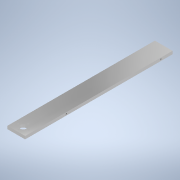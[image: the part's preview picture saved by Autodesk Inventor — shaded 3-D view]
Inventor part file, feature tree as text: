
AUTODESK INVENTOR PART (.ipt)
format: ipt  version: 2022 (Build 260153000, 153)  size: 126,464 bytes
history: native  units: mm
features: sketch x4, hole x3, other x1, extrude x1
ambient origin geometry x8: Origin, YZ Plane, XZ Plane, XY Plane, X Axis, Y Axis, Z Axis, Center Point
bodies: Body1 (feature_tree)
feature tree (9):
  other  "ソリッド1"
  extrude  "押し出し1"  Depth=250.0mm
  hole  "穴1"  [1 undecoded]
  hole  "穴2"  [1 undecoded]
  hole  "穴3"  [1 undecoded]
  sketch  "スケッチ1"
  sketch  "スケッチ2"
  sketch  "スケッチ3"
  sketch  "スケッチ4"
note: 3 required parameter values undecoded (feature->parameter linkage not recoverable at this tier; creation-order binding heuristic only, values carry confidence <= 0.55)
